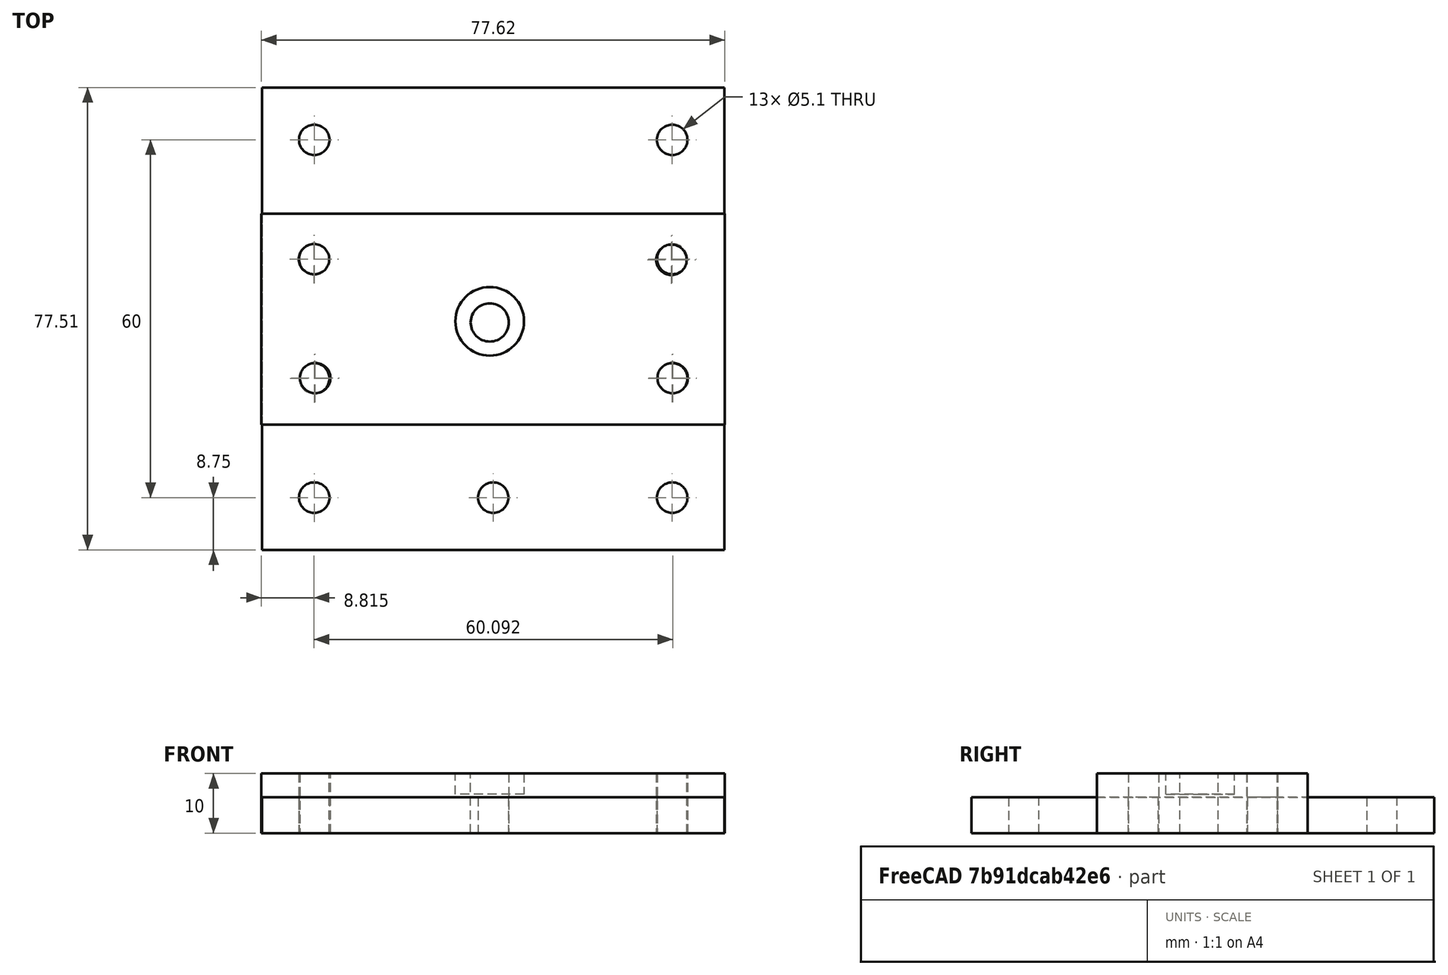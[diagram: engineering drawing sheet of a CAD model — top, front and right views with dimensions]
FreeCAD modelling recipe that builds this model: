
FCSTD DOCUMENT  (FreeCAD 0.14R2935 (Git))
Label: C-beam gantry plate
License: CC-BY 3.0
LicenseURL: http://creativecommons.org/licenses/by/3.0/
objects: Sketcher::SketchObject×4, PartDesign::Pad×2, PartDesign::Pocket×2, Mesh::Feature×1
note: 12 computed .brp shape members not serialized (recipe doc carries the construction recipe); baked Part::Feature solids carry a one-line shape summary decoded from their .brp

FEATURE [Mesh::Feature] C_Beam_Gantry_Plate_V1_STL  label="C-Beam_Gantry Plate_V1_STL"
FEATURE [Sketcher::SketchObject] Sketch
  Placement = pos=(77.6,0,0) rot=(0,0,1;1.5708rad)
  sketch-geometry (14):
    g0: LineSegment StartX=0 StartY=0 StartZ=0 EndX=77.51 EndY=0 EndZ=0
    g1: LineSegment StartX=77.51 StartY=0 StartZ=0 EndX=77.51 EndY=77.51 EndZ=0
    g2: LineSegment StartX=77.51 StartY=77.51 StartZ=0 EndX=0 EndY=77.51 EndZ=0
    g3: LineSegment StartX=0 StartY=77.51 StartZ=0 EndX=0 EndY=0 EndZ=0
    g4: Circle CenterX=8.75 CenterY=68.76 CenterZ=0 NormalX=0 NormalY=0 NormalZ=1 Radius=2.55
    g5: Circle CenterX=8.76 CenterY=38.76 CenterZ=0 NormalX=0 NormalY=0 NormalZ=1 Radius=2.55
    g6: Circle CenterX=8.76 CenterY=8.76 CenterZ=0 NormalX=0 NormalY=0 NormalZ=1 Radius=2.55
    g7: Circle CenterX=28.75 CenterY=68.75 CenterZ=0 NormalX=0 NormalY=0 NormalZ=1 Radius=2.55
    g8: Circle CenterX=48.75 CenterY=68.75 CenterZ=0 NormalX=0 NormalY=0 NormalZ=1 Radius=2.55
    g9: Circle CenterX=68.75 CenterY=68.75 CenterZ=0 NormalX=0 NormalY=0 NormalZ=1 Radius=2.55
    g10: Circle CenterX=68.75 CenterY=8.76 CenterZ=0 NormalX=0 NormalY=0 NormalZ=1 Radius=2.55
    g11: Circle CenterX=48.76 CenterY=8.76 CenterZ=0 NormalX=0 NormalY=0 NormalZ=1 Radius=2.55
    g12: Circle CenterX=28.76 CenterY=8.76 CenterZ=0 NormalX=0 NormalY=0 NormalZ=1 Radius=2.55
    g13: Circle CenterX=68.75 CenterY=38.76 CenterZ=0 NormalX=0 NormalY=0 NormalZ=1 Radius=2.55
  constraints (42):
    c: Coincident(g0,g1)
    c: Coincident(g1,g2)
    c: Coincident(g2,g3)
    c: Coincident(g3,g0)
    c: Horizontal(g0)
    c: Horizontal(g2)
    c: Vertical(g1)
    c: Vertical(g3)
    c: Coincident(g0,g-1)
    c: DistanceY(g-1,g2) = 77.51
    c: DistanceX(g2,g1) = 77.51
    c: DistanceY(g4) = 68.76
    c: Radius(g4) = 2.55
    c: Radius(g5) = 2.55
    c: Radius(g6) = 2.55
    c: Radius(g7) = 2.55
    c: DistanceY(g-1,g6) = 8.76
    c: DistanceY(g-1,g5) = 38.76
    c: Radius(g8) = 2.55
    c: DistanceX(g-1,g6) = 8.76
    c: DistanceX(g-1,g5) = 8.76
    c: Distance(g4,g7) = 20
    c: Distance(g7,g8) = 20
    c: DistanceY(g7,g2) = 8.76
    c: DistanceY(g8,g1) = 8.76
    c: DistanceX(g9,g8) = -20
    c: Radius(g9) = 2.55
    c: DistanceY(g1,g9) = -8.76
    c: DistanceX(g1,g9) = -8.76
    c: Radius(g10) = 2.55
    c: DistanceY(g10,g0) = -8.76
    c: DistanceX(g10,g0) = 8.76
    c: Radius(g12) = 2.55
    c: Radius(g11) = 2.55
    c: DistanceY(g11,g0) = -8.76
    c: DistanceY(g12,g0) = -8.76
    c: DistanceX(g12,g6) = -20
    c: DistanceX(g12,g11) = 20
    c: DistanceX(g10) = 68.75
    c: Radius(g13) = 2.55
    c: DistanceY(g13,g0) = -38.76
    c: DistanceX(g13,g1) = 8.76
FEATURE [PartDesign::Pad] Pad
  Length = 6
  Length2 = 100
  Placement = pos=(77.6,0,0) rot=(0,0,1;1.5708rad)
  Sketch = -> Sketch
  Type = 0
FEATURE [Sketcher::SketchObject] Sketch001
  sketch-geometry (8):
    g0: LineSegment StartX=0 StartY=56.3455 StartZ=0 EndX=77.6203 EndY=56.3455 EndZ=0
    g1: LineSegment StartX=77.6203 StartY=56.3455 StartZ=0 EndX=77.6203 EndY=20.9913 EndZ=0
    g2: LineSegment StartX=77.6203 StartY=20.9913 StartZ=0 EndX=0 EndY=20.9913 EndZ=0
    g3: LineSegment StartX=0 StartY=20.9913 StartZ=0 EndX=0 EndY=56.3455 EndZ=0
    g4: Circle CenterX=8.81479 CenterY=48.7338 CenterZ=0 NormalX=0 NormalY=0 NormalZ=1 Radius=2.55
    g5: Circle CenterX=68.7066 CenterY=48.6337 CenterZ=0 NormalX=0 NormalY=0 NormalZ=1 Radius=2.55
    g6: Circle CenterX=68.9069 CenterY=28.8033 CenterZ=0 NormalX=0 NormalY=0 NormalZ=1 Radius=2.55
    g7: Circle CenterX=9.0151 CenterY=28.8033 CenterZ=0 NormalX=0 NormalY=0 NormalZ=1 Radius=2.55
  constraints (13):
    c: Coincident(g0,g1)
    c: Coincident(g1,g2)
    c: Coincident(g2,g3)
    c: Coincident(g3,g0)
    c: Horizontal(g0)
    c: Horizontal(g2)
    c: Vertical(g1)
    c: Vertical(g3)
    c: PointOnObject(g0,g-2)
    c: Radius(g4) = 2.55
    c: Radius(g6) = 2.55
    c: Radius(g5) = 2.55
    c: Radius(g7) = 2.55
FEATURE [PartDesign::Pad] Pad001
  Length = 10
  Length2 = 100
  Sketch = -> Sketch001
  Type = 0
FEATURE [Sketcher::SketchObject] Sketch002
  Placement = pos=(0,0,10) rot=(0,0,1;0rad)
  Support = -> Pad001 [Face10]
  sketch-geometry (1):
    g0: Circle CenterX=38.26 CenterY=38.1175 CenterZ=0 NormalX=0 NormalY=0 NormalZ=1 Radius=3.2
  constraints (1):
    c: Radius(g0) = 3.2
FEATURE [PartDesign::Pocket] Pocket
  Length = 10
  Sketch = -> Sketch002
  Type = 0
FEATURE [Sketcher::SketchObject] Sketch003
  Placement = pos=(0,0,10) rot=(0,0,1;0rad)
  Support = -> Pad001 [Face10]
  sketch-geometry (1):
    g0: Circle CenterX=38.26 CenterY=38.3179 CenterZ=0 NormalX=0 NormalY=0 NormalZ=1 Radius=5.75
  constraints (1):
    c: Radius(g0) = 5.75
FEATURE [PartDesign::Pocket] Pocket001
  Length = 3.5
  Sketch = -> Sketch003
  Type = 0
